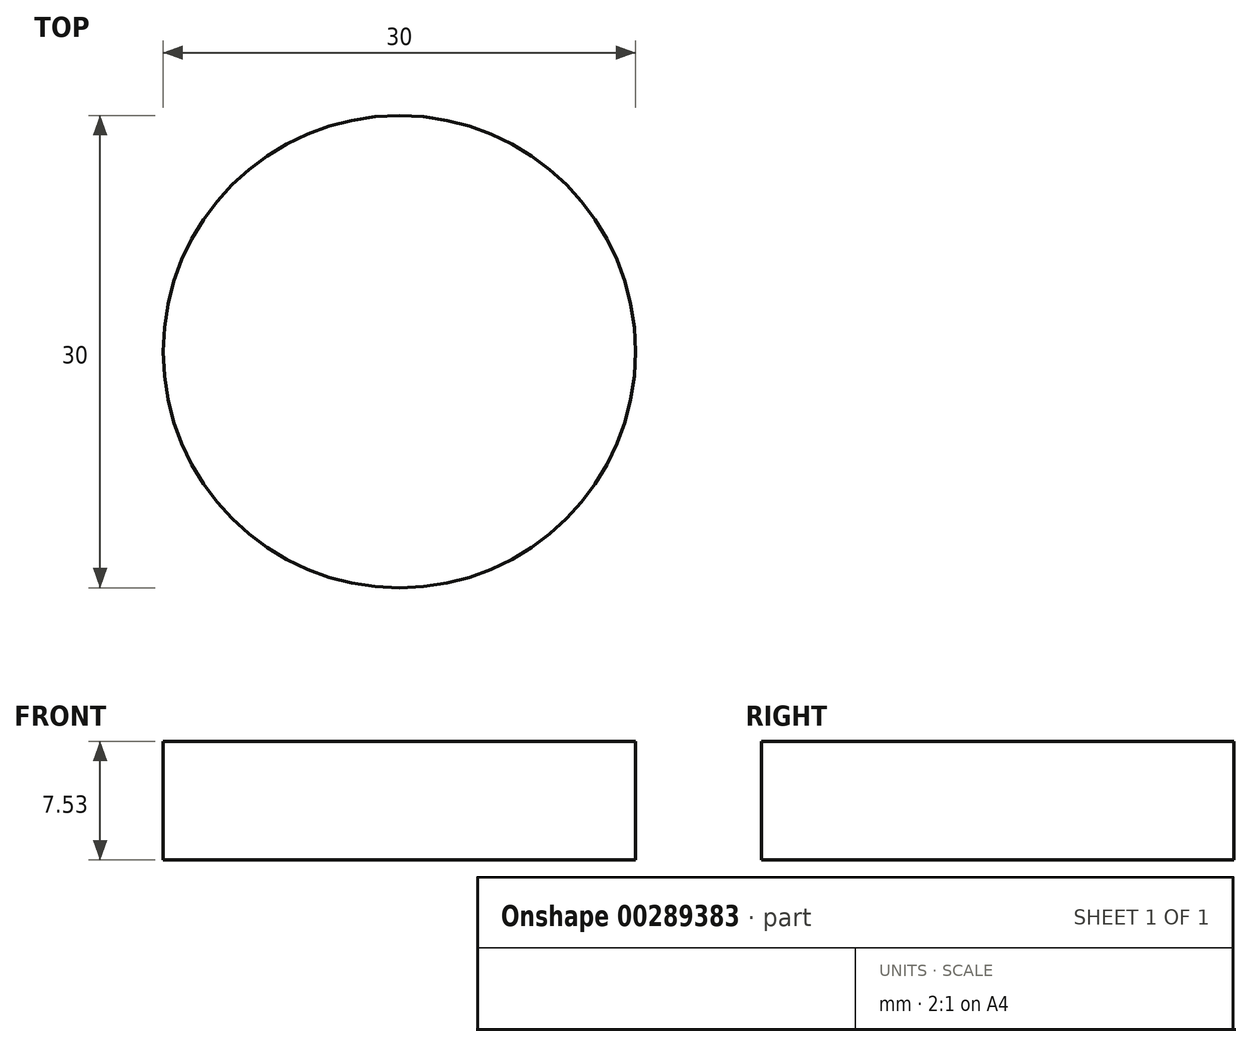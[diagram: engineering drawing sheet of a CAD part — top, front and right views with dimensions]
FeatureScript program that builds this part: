
annotation { "Feature Type Name" : "Feature", "Feature Type Description" : "" }
export const myFeature = defineFeature(function(context is Context, id is Id, definition is map)
    precondition{}
    {
        {
            var Q0;
            Q0=qCreatedBy(makeId("Top.planeOp"),FACE);
            var sketch = newSketch(context, id + "F0", { "sketchPlane" : qUnion([Q0])});
            skCircle(sketch, "E0", {"center": v(0, 0) * mm, "radius": 15 * mm});
            skSolve(sketch);
        }
        {
            var Q0;
            Q0 = qSketchRegion(id + "F0", true);
            extrude(context, id + "F1", {"entities" : qUnion([Q0]), "depth" : 30 * mm});
        }
        {
            var Q0;
            Q0=qCreatedBy(makeId("Right.planeOp"),FACE);
            var sketch = newSketch(context, id + "F2", { "sketchPlane" : qUnion([Q0])});
            skLineSegment(sketch, "E1", {"start": v(28, 37.14) * mm, "end": v(28, 7.53) * mm});
            skLineSegment(sketch, "E2", {"start": v(28, 7.53) * mm, "end": v(-31.33, 7.53) * mm});
            skLineSegment(sketch, "E3", {"start": v(-31.33, 7.53) * mm, "end": v(-31.33, 34.9) * mm});
            skLineSegment(sketch, "E4", {"start": v(-31.33, 34.9) * mm, "end": v(28, 37.14) * mm});
            skSolve(sketch);
        }
        {
            var Q0;
            Q0=makeQuery(id+"F2.imprint","IMPRINT",FACE,{"disambiguationData":[TD([[makeQuery(id+"F2.imprint","IMPRINT",EDGE,{"derivedFrom":sQuery(id+"F2.wireOp",EDGE,"E1")}),-1.0]])]});
            extrude(context, id + "F3", {"entities" : qUnion([Q0]), "operationType" : NewBodyOperationType.REMOVE, "endBound" : BoundingType.SYMMETRIC, "oppositeDirection" : true, "depth" : 50 * mm});
        }
    });
